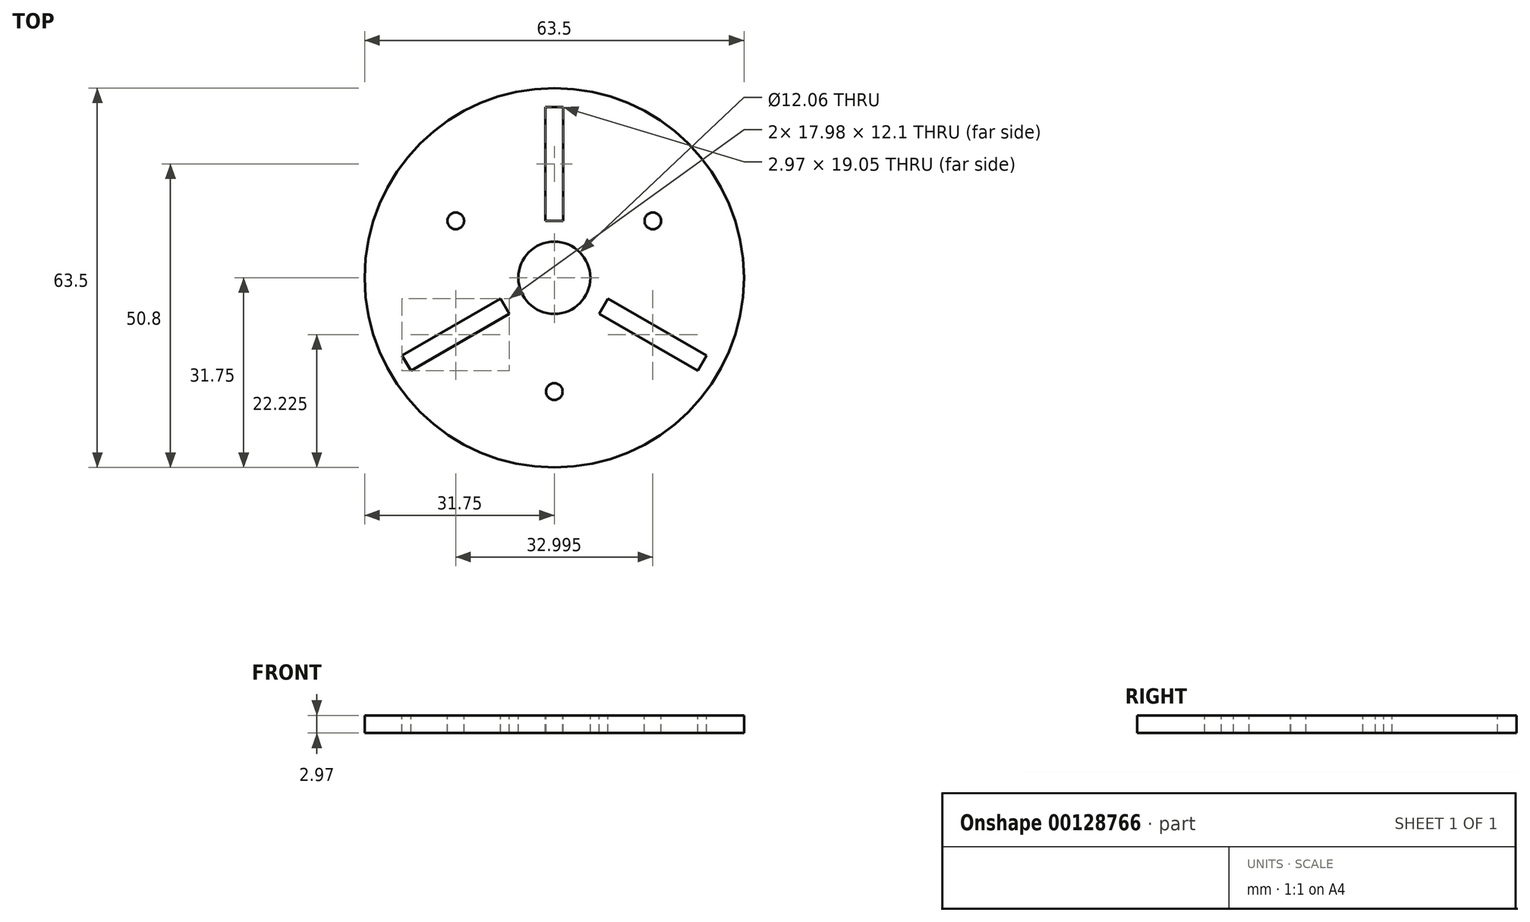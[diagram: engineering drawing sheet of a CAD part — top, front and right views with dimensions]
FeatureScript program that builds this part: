
annotation { "Feature Type Name" : "Feature", "Feature Type Description" : "" }
export const myFeature = defineFeature(function(context is Context, id is Id, definition is map)
    precondition{}
    {
        {
            var Q0;
            Q0=qCreatedBy(makeId("Top.planeOp"),FACE);
            var sketch = newSketch(context, id + "F0", { "sketchPlane" : qUnion([Q0])});
            skCircle(sketch, "E0", {"center": v(0, 0) * mm, "radius": 31.75 * mm});
            skSolve(sketch);
        }
        {
            var Q0;
            Q0=makeQuery(id+"F0.imprint","IMPRINT",FACE,{"disambiguationData":[TD([[makeQuery(id+"F0.imprint","IMPRINT",EDGE,{"derivedFrom":sQuery(id+"F0.wireOp",EDGE,"E0")}),1.0]])]});
            extrude(context, id + "F1", {"entities" : qUnion([Q0]), "oppositeDirection" : true, "depth" : 2.97 * mm});
        }
        {
            var Q0;
            Q0=makeQuery(id+"F1.opExtrude","CAP_FACE",FACE,{"disambiguationData":[OSD([sQuery(id+"F0.wireOp",EDGE,"E0")])],"isStart":true});
            var sketch = newSketch(context, id + "F2", { "sketchPlane" : qUnion([Q0])});
            skLineSegment(sketch, "E1.bottom", {"start": v(1.49, 9.53) * mm, "end": v(-1.49, 9.53) * mm});
            skLineSegment(sketch, "E1.top", {"start": v(1.49, 28.57) * mm, "end": v(-1.49, 28.57) * mm});
            skLineSegment(sketch, "E1.left", {"start": v(1.49, 9.53) * mm, "end": v(1.49, 28.57) * mm});
            skLineSegment(sketch, "E1.right", {"start": v(-1.49, 9.53) * mm, "end": v(-1.49, 28.57) * mm});
            skLineSegment(sketch, "E2", {"start": v(7.5, -6.05) * mm, "end": v(24, -15.57) * mm});
            skLineSegment(sketch, "E3", {"start": v(24, -15.57) * mm, "end": v(25.49, -13) * mm});
            skLineSegment(sketch, "E4", {"start": v(25.49, -13) * mm, "end": v(9, -3.48) * mm});
            skLineSegment(sketch, "E5", {"start": v(9, -3.48) * mm, "end": v(7.5, -6.05) * mm});
            skLineSegment(sketch, "E6", {"start": v(-9, -3.48) * mm, "end": v(-7.5, -6.05) * mm});
            skLineSegment(sketch, "E7", {"start": v(-7.5, -6.05) * mm, "end": v(-24, -15.57) * mm});
            skLineSegment(sketch, "E8", {"start": v(-24, -15.57) * mm, "end": v(-25.49, -13) * mm});
            skLineSegment(sketch, "E9", {"start": v(-25.49, -13) * mm, "end": v(-9, -3.48) * mm});
            skPoint(sketch, "E10", {"position": v(0, 28.57) * mm});
            skPoint(sketch, "E11", {"position": v(-24.75, -14.29) * mm});
            skPoint(sketch, "E12", {"position": v(24.75, -14.29) * mm});
            skPoint(sketch, "E13", {"position": v(-8.25, -4.76) * mm});
            skPoint(sketch, "E14", {"position": v(8.25, -4.76) * mm});
            skPoint(sketch, "E15", {"position": v(0, 9.53) * mm});
            skLineSegment(sketch, "E16", {"start": v(-8.25, -4.76) * mm, "end": v(0, 0) * mm, "construction": true});
            skLineSegment(sketch, "E17", {"start": v(0, 9.53) * mm, "end": v(0, 0) * mm, "construction": true});
            skLineSegment(sketch, "E18", {"start": v(0, 0) * mm, "end": v(8.25, -4.76) * mm, "construction": true});
            skCircle(sketch, "E19", {"center": v(0, 0) * mm, "radius": 6.03 * mm});
            skCircle(sketch, "E20", {"center": v(-16.5, 9.52) * mm, "radius": 1.4 * mm});
            skCircle(sketch, "E21", {"center": v(16.5, 9.52) * mm, "radius": 1.4 * mm});
            skCircle(sketch, "E22", {"center": v(0, -19.05) * mm, "radius": 1.4 * mm});
            skLineSegment(sketch, "E23", {"start": v(0, 0) * mm, "end": v(0, -19.05) * mm, "construction": true});
            skLineSegment(sketch, "E24", {"start": v(0, 0) * mm, "end": v(16.5, 9.52) * mm, "construction": true});
            skLineSegment(sketch, "E25", {"start": v(0, 0) * mm, "end": v(-16.5, 9.52) * mm, "construction": true});
            skSolve(sketch);
        }
        {
            var Q0;
            Q0=makeQuery(id+"F2.imprint","IMPRINT",FACE,{"disambiguationData":[TD([[makeQuery(id+"F2.imprint","IMPRINT",EDGE,{"derivedFrom":sQuery(id+"F2.wireOp",EDGE,"E19")}),1.0]])]});
            var Q1;
            Q1=makeQuery(id+"F2.imprint","IMPRINT",FACE,{"disambiguationData":[TD([[makeQuery(id+"F2.imprint","IMPRINT",EDGE,{"derivedFrom":sQuery(id+"F2.wireOp",EDGE,"E1.bottom")}),-1.0]])]});
            var Q2;
            Q2=makeQuery(id+"F2.imprint","IMPRINT",FACE,{"disambiguationData":[TD([[makeQuery(id+"F2.imprint","IMPRINT",EDGE,{"derivedFrom":sQuery(id+"F2.wireOp",EDGE,"E6")}),-1.0]])]});
            var Q3;
            Q3=makeQuery(id+"F2.imprint","IMPRINT",FACE,{"disambiguationData":[TD([[makeQuery(id+"F2.imprint","IMPRINT",EDGE,{"derivedFrom":sQuery(id+"F2.wireOp",EDGE,"E2")}),1.0]])]});
            var Q4;
            Q4=makeQuery(id+"F2.imprint","IMPRINT",FACE,{"disambiguationData":[TD([[makeQuery(id+"F2.imprint","IMPRINT",EDGE,{"derivedFrom":sQuery(id+"F2.wireOp",EDGE,"E20")}),1.0]])]});
            var Q5;
            Q5=makeQuery(id+"F2.imprint","IMPRINT",FACE,{"disambiguationData":[TD([[makeQuery(id+"F2.imprint","IMPRINT",EDGE,{"derivedFrom":sQuery(id+"F2.wireOp",EDGE,"E21")}),1.0]])]});
            var Q6;
            Q6=makeQuery(id+"F2.imprint","IMPRINT",FACE,{"disambiguationData":[TD([[makeQuery(id+"F2.imprint","IMPRINT",EDGE,{"derivedFrom":sQuery(id+"F2.wireOp",EDGE,"E22")}),1.0]])]});
            var Q7;
            Q7=makeQuery(id+"F1.opExtrude","CAP_FACE",FACE,{"disambiguationData":[OSD([sQuery(id+"F0.wireOp",EDGE,"E0")])],"isStart":false});
            extrude(context, id + "F3", {"entities" : qUnion([Q0, Q1, Q2, Q3, Q4, Q5, Q6]), "operationType" : NewBodyOperationType.REMOVE, "endBound" : BoundingType.UP_TO_SURFACE, "oppositeDirection" : true, "endBoundEntityFace" : qUnion([Q7]), "depth" : 25.4 * mm});
        }
    });
